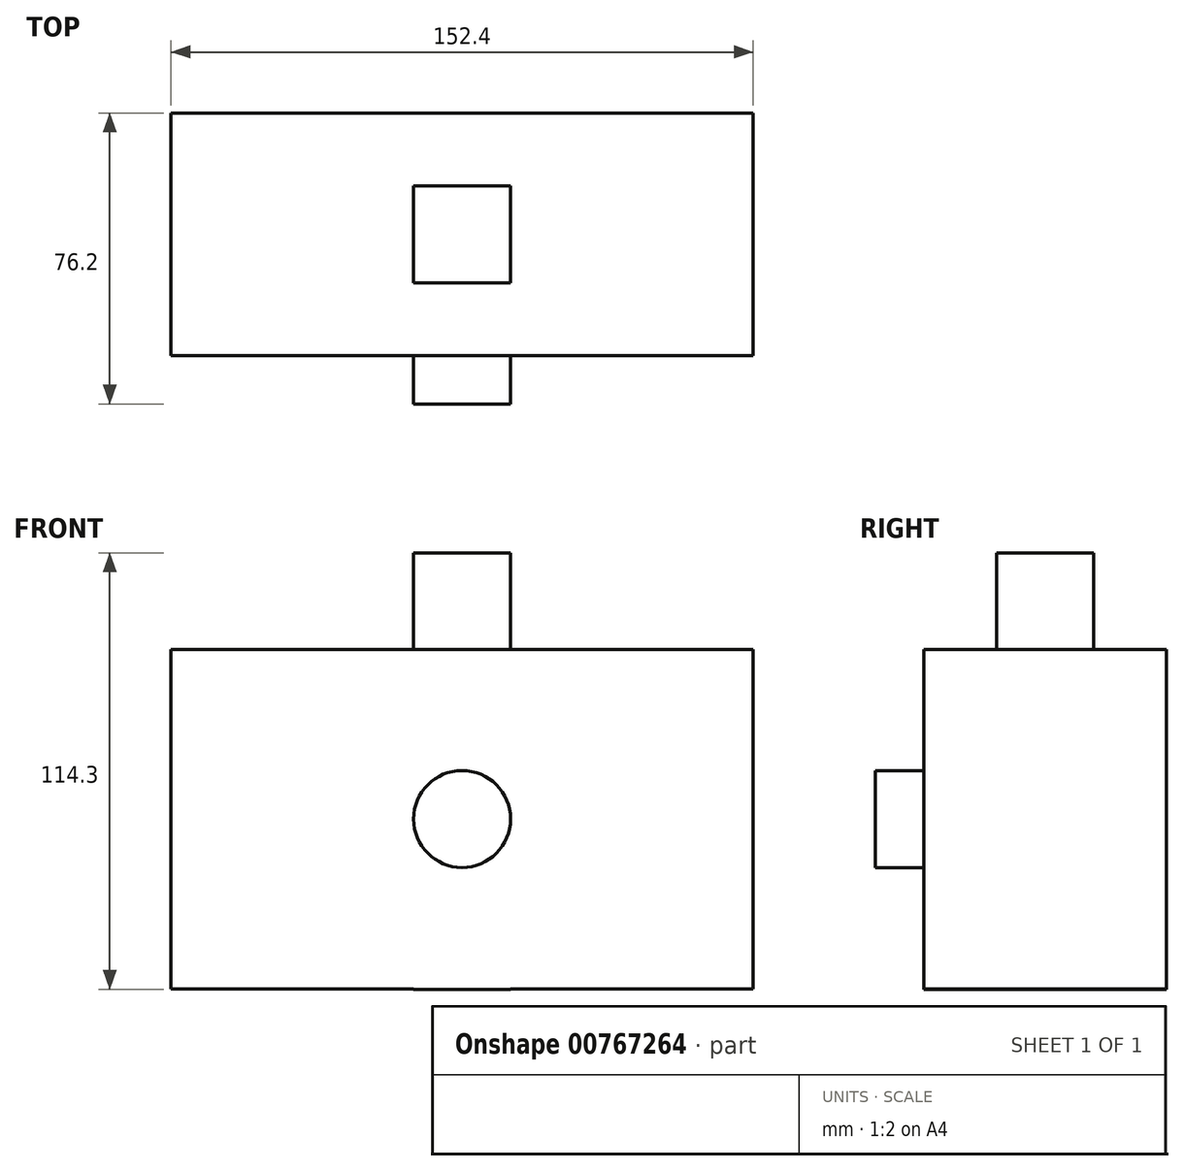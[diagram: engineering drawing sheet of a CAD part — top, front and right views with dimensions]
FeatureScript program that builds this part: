
annotation { "Feature Type Name" : "Feature", "Feature Type Description" : "" }
export const myFeature = defineFeature(function(context is Context, id is Id, definition is map)
    precondition{}
    {
        {
            var Q0;
            Q0=qCreatedBy(makeId("Front.planeOp"),FACE);
            var sketch = newSketch(context, id + "F0", { "sketchPlane" : qUnion([Q0])});
            skLineSegment(sketch, "E0.bottom", {"start": v(-76.2, 44.45) * mm, "end": v(76.2, 44.45) * mm});
            skLineSegment(sketch, "E0.top", {"start": v(-76.2, -44.45) * mm, "end": v(76.2, -44.45) * mm});
            skLineSegment(sketch, "E0.left", {"start": v(-76.2, 44.45) * mm, "end": v(-76.2, -44.45) * mm});
            skLineSegment(sketch, "E0.right", {"start": v(76.2, 44.45) * mm, "end": v(76.2, -44.45) * mm});
            skPoint(sketch, "E0.middle", {"position": v(0, 0) * mm});
            skCircle(sketch, "E1", {"center": v(0, 0) * mm, "radius": 12.7 * mm});
            skLineSegment(sketch, "E2.bottom", {"start": v(-12.7, 44.45) * mm, "end": v(12.7, 44.45) * mm});
            skLineSegment(sketch, "E2.top", {"start": v(-12.7, 69.85) * mm, "end": v(12.7, 69.85) * mm});
            skLineSegment(sketch, "E2.left", {"start": v(-12.7, 44.45) * mm, "end": v(-12.7, 69.85) * mm});
            skLineSegment(sketch, "E2.right", {"start": v(12.7, 44.45) * mm, "end": v(12.7, 69.85) * mm});
            skSolve(sketch);
        }
        {
            var Q0;
            Q0=makeQuery(id+"F0.imprint","IMPRINT",FACE,{"disambiguationData":[TD([[makeQuery(id+"F0.imprint","IMPRINT",EDGE,{"derivedFrom":sQuery(id+"F0.wireOp",EDGE,"E0.top")}),1.0]])]});
            extrude(context, id + "F1", {"entities" : qUnion([Q0]), "depth" : 63.5 * mm, "offsetDistance" : 25.4 * mm});
        }
        {
            var Q0;
            Q0=makeQuery(id+"F0.imprint","IMPRINT",FACE,{"disambiguationData":[TD([[makeQuery(id+"F0.imprint","IMPRINT",EDGE,{"derivedFrom":sQuery(id+"F0.wireOp",EDGE,"E1")}),1.0]])]});
            var Q1;
            Q1=makeQuery(id+"F1.opExtrude","SWEPT_BODY",BODY,{"disambiguationData":[OSD([sQuery(id+"F0.wireOp",EDGE,"E0.bottom"),sQuery(id+"F0.wireOp",EDGE,"E0.top"),sQuery(id+"F0.wireOp",EDGE,"E0.left"),sQuery(id+"F0.wireOp",EDGE,"E0.right"),sQuery(id+"F0.wireOp",EDGE,"E1"),sQuery(id+"F0.wireOp",EDGE,"E2.bottom")])]});
            extrude(context, id + "F2", {"entities" : qUnion([Q0]), "operationType" : NewBodyOperationType.ADD, "depth" : 76.2 * mm, "endBoundEntityBody" : qUnion([Q1]), "offsetDistance" : 25.4 * mm});
        }
        {
            var Q0;
            Q0=qCreatedBy(makeId("Right.planeOp"),FACE);
            var sketch = newSketch(context, id + "F3", { "sketchPlane" : qUnion([Q0])});
            skLineSegment(sketch, "E3.bottom", {"start": v(-63.5, 44.32) * mm, "end": v(0, 44.32) * mm});
            skLineSegment(sketch, "E3.top", {"start": v(-63.5, -44.58) * mm, "end": v(0, -44.58) * mm});
            skLineSegment(sketch, "E3.left", {"start": v(-63.5, 44.32) * mm, "end": v(-63.5, -44.58) * mm});
            skLineSegment(sketch, "E3.right", {"start": v(0, 44.32) * mm, "end": v(0, -44.58) * mm});
            skLineSegment(sketch, "E4.bottom", {"start": v(-44.45, 44.32) * mm, "end": v(-19.05, 44.32) * mm});
            skLineSegment(sketch, "E4.top", {"start": v(-44.45, 69.72) * mm, "end": v(-19.05, 69.72) * mm});
            skLineSegment(sketch, "E4.left", {"start": v(-44.45, 44.32) * mm, "end": v(-44.45, 69.72) * mm});
            skLineSegment(sketch, "E4.right", {"start": v(-19.05, 44.32) * mm, "end": v(-19.05, 69.72) * mm});
            skSolve(sketch);
        }
        {
            var Q0;
            Q0 = qSketchRegion(id + "F3", true);
            extrude(context, id + "F4", {"entities" : qUnion([Q0]), "operationType" : NewBodyOperationType.ADD, "endBound" : BoundingType.SYMMETRIC, "depth" : 25.4 * mm, "offsetDistance" : 25.4 * mm});
        }
    });
